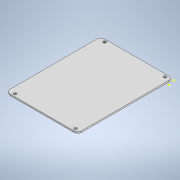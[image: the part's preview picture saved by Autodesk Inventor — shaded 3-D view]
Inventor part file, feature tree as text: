
AUTODESK INVENTOR PART (.ipt)
format: ipt  version: 2022 (Build 260153000, 153)  size: 582,144 bytes
history: native  units: mm
features: extrude x25, sketch x25, projected_geometry x10
ambient origin geometry x8: Origin, YZ Plane, XZ Plane, XY Plane, X Axis, Y Axis, Z Axis, Center Point
bodies: Body1 (feature_tree)
feature tree (60):
  extrude  "Extrusion8"  Depth=3.0mm TaperAngle=0.0deg
  extrude  "Extrusion9"  Depth=71.5mm
  extrude  "Extrusion10"  Depth=8.0mm
  extrude  "Extrusion11"  Depth=8.0mm
  extrude  "Extrusion12"  Depth=6.0mm
  extrude  "Extrusion13"  Depth=8.14mm
  extrude  "Extrusion14"  Depth=7.1mm
  sketch  "Sketch19"  dims[d82=6.0mm d83=7.1mm]
  extrude  "Extrusion16"  Depth=7.0mm
  extrude  "Extrusion17"  Depth=2.5mm
  extrude  "Extrusion18"  Depth=1.0mm
  extrude  "Extrusion19"  Depth=1.5mm
  extrude  "Extrusion20"  Depth=9.0mm TaperAngle=0.0deg
  extrude  "Extrusion21"  Depth=2.0mm
  extrude  "Extrusion24"  Depth=2.0mm
  extrude  "Extrusion25"  Depth=3.0mm TaperAngle=0.0deg
  sketch  "Sketch34"  dims[d117=3.0mm d118=3.0mm]
  extrude  "Extrusion26"  Depth=3.0mm
  extrude  "Extrusion27"  Depth=3.0mm
  extrude  "Extrusion28"  TaperAngle=0.0deg  [1 undecoded]
  extrude  "Extrusion29"  Depth=15.5mm
  extrude  "Extrusion30"  Depth=20.5mm
  extrude  "Extrusion31"  Depth=8.0mm
  extrude  "Extrusion32"  Depth=8.0mm
  extrude  "Extrusion33"  Depth=5.0mm
  extrude  "Extrusion34"  Depth=8.0mm TaperAngle=0.0deg
  extrude  "Extrusion35"  Depth=2.5mm
  sketch  "Sketch12"  dims[d68=3.0mm d69=0.0mm d70=3.0mm d71=0.0mm]
  projected_geometry  "Projected Loop1"
  projected_geometry  "Projected Loop2"
  sketch  "Sketch14"  dims[d72=71.5mm d73=67.15mm]
  sketch  "Sketch15"  dims[d74=8.0mm d75=8.0mm]
  sketch  "Sketch16"  dims[d76=8.0mm d77=8.0mm]
  sketch  "Sketch17"  dims[d78=6.0mm d79=11.8mm]
  sketch  "Sketch18"  dims[d80=6.8mm d81=8.14mm]
  sketch  "Sketch21"  dims[d84=6.0mm d85=7.0mm]
  projected_geometry  "Projected Loop3"
  sketch  "Sketch22"  dims[d86=3.0mm d87=0.0mm d88=2.5mm]
  projected_geometry  "Projected Loop4"
  projected_geometry  "Projected Loop5"
  sketch  "Sketch23"  dims[d89=3.0mm d90=0.0mm d91=1.0mm]
  sketch  "Sketch25"  dims[d92=1.5mm d93=0.0mm d94=5.65mm]
  sketch  "Sketch26"  dims[d95=9.0mm d96=11.17mm d97=0.0mm]
  sketch  "Sketch27"  dims[d98=2.0mm d99=2.0mm]
  sketch  "Sketch32"  dims[d100=2.5mm d101=0.0mm d112=2.0mm]
  sketch  "Sketch33"  dims[d113=2.0mm d114=0.0mm d115=3.0mm d116=0.0mm]
  sketch  "Sketch35"  dims[d119=3.0mm d120=3.0mm]
  sketch  "Sketch37"  dims[d121=0.5mm d122=0.0mm d123=0.0mm]
  sketch  "Sketch38"  dims[d124=0.0mm d125=15.5mm]
  sketch  "Sketch39"  dims[d126=0.0mm d127=20.5mm]
  sketch  "Sketch40"  dims[d128=8.0mm d129=8.0mm]
  projected_geometry  "Projected Loop6"
  sketch  "Sketch41"  dims[d130=8.0mm d131=8.0mm]
  sketch  "Sketch43"  dims[d132=5.3mm d133=5.0mm]
  sketch  "Sketch44"  dims[d134=0.0mm d135=8.0mm d136=0.0mm]
  sketch  "Sketch47"  dims[d137=8.0mm d138=0.0mm d139=2.5mm d140=2.5mm d141=2.5mm d142=2.5mm d143=6.0mm d144=0.0mm d160=100.0mm d161=0.0mm d162=10.0mm d163=0.0mm d164=14.5mm d166=0.74mm d167=100.0mm d168=0.0mm d170=2.5mm d171=2.5mm d172=2.5mm d173=2.5mm d174=5.0mm d175=0.0mm d176=8.0mm d177=8.0mm d178=8.0mm d179=8.0mm d181=53.0mm d182=17.3mm d183=2.0mm d184=2.0mm d185=7.6mm d186=2.1mm d187=2.1mm d190=10.0mm d191=20.0mm d192=3.0mm d193=0.0mm d194=2.5mm d195=2.5mm d196=2.5mm d197=2.5mm d198=5.0mm d199=0.0mm d200=8.0mm d201=8.0mm d202=8.3mm d203=10.0mm d204=10.0mm d205=1.9mm d206=0.0mm d207=10.0mm d208=0.0mm d209=2.5mm d211=2.5mm d212=4.0mm d213=0.0mm d216=22.55489mm d217=8.861037mm d218=2.582mm d219=4.0mm d220=0.0mm d221=8.588357mm d222=5.0mm d223=5.0mm d224=0.0mm d225=10.0mm d226=0.0mm d227=2.85mm d228=14.0mm d229=20.0mm d230=4.0mm d237=68.0mm d239=13.7mm d240=14.9mm d241=4.0mm d242=4.0mm d243=4.0mm d244=4.0mm d245=2.0mm d246=0.0mm d165=0.872665mm]
  projected_geometry  "Projected Loop7"
  projected_geometry  "Projected Loop8"
  projected_geometry  "Projected Loop9"
  projected_geometry  "Projected Loop10"
note: 1 required parameter value undecoded (feature->parameter linkage not recoverable at this tier; creation-order binding heuristic only, values carry confidence <= 0.55)
